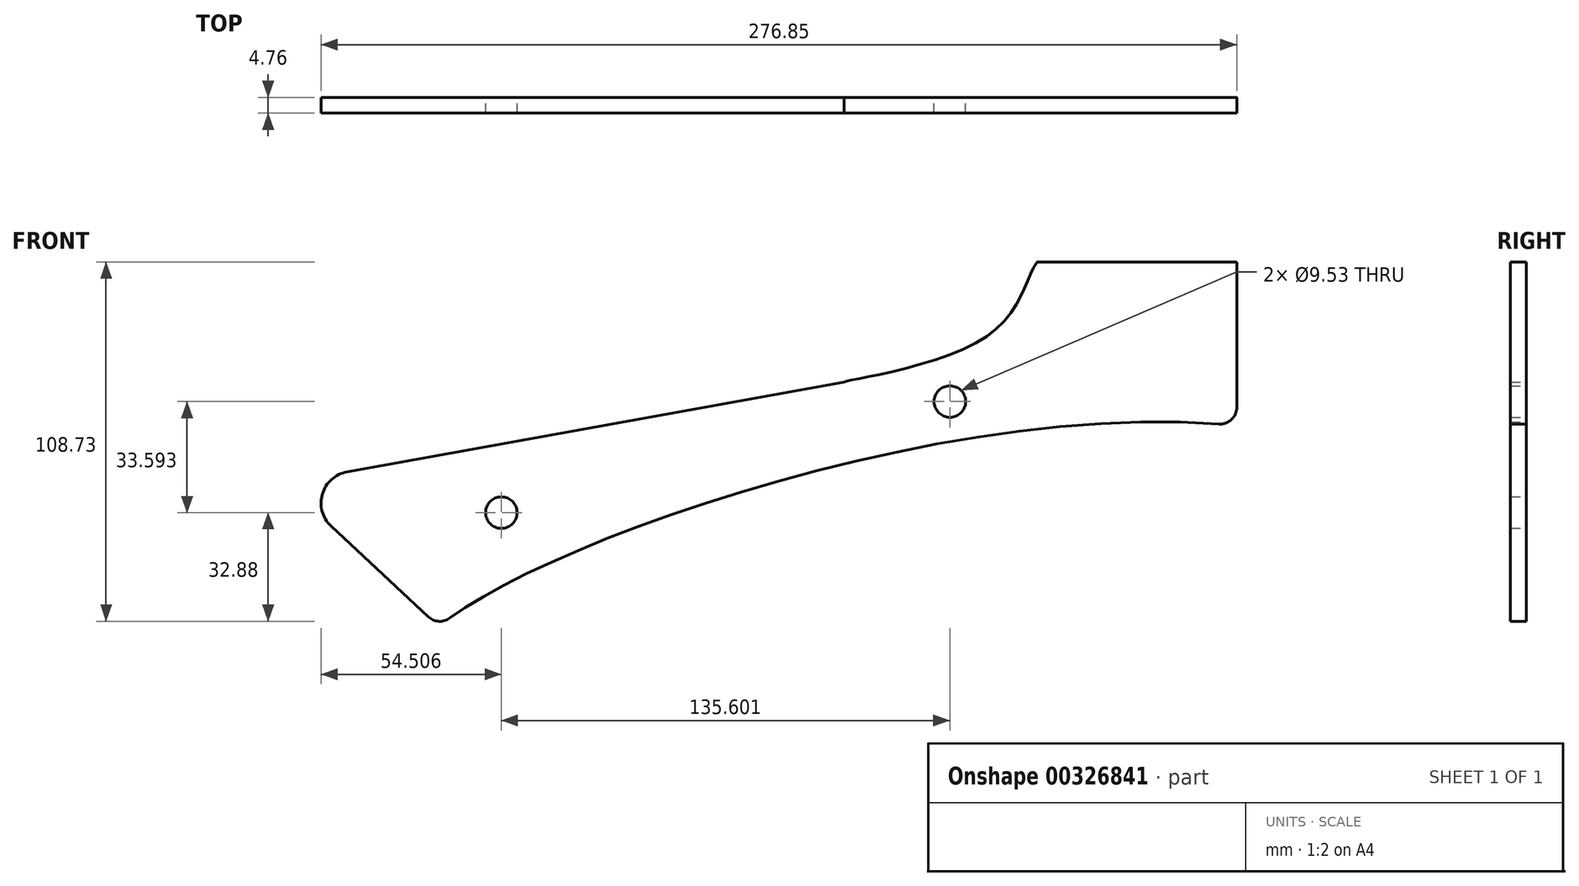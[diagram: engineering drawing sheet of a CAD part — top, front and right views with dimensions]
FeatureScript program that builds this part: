
annotation { "Feature Type Name" : "Feature", "Feature Type Description" : "" }
export const myFeature = defineFeature(function(context is Context, id is Id, definition is map)
    precondition{}
    {
        {
            var Q0;
            Q0=qCreatedBy(makeId("Front.planeOp"),FACE);
            var sketch = newSketch(context, id + "F0", { "sketchPlane" : qUnion([Q0])});
            skLineSegment(sketch, "E0", {"start": v(-108.84, -14.05) * mm, "end": v(-62.45, -57.41) * mm});
            skFitSpline(sketch, "E1", {"points": [v(-62.45, -57.41) * mm, v(6.41, -24.14) * mm, v(178.85, 3.34) * mm], "startDerivative": vector(92.55, 74.48) * mm, "endDerivative": vector(274.58, -28.19) * mm});
            skLineSegment(sketch, "E2", {"start": v(178.85, 3.34) * mm, "end": v(178.85, 52.87) * mm});
            skLineSegment(sketch, "E3", {"start": v(178.85, 52.87) * mm, "end": v(118.52, 52.87) * mm});
            skCircle(sketch, "E4", {"center": v(-43.5, -22.98) * mm, "radius": 4.76 * mm});
            skCircle(sketch, "E5", {"center": v(92.1, 10.61) * mm, "radius": 4.76 * mm});
            skPoint(sketch, "E6.1.internal.orphan", {"position": v(26.94, 0) * mm});
            skFitSpline(sketch, "E7", {"points": [v(118.52, 52.87) * mm, v(103.5, 30.5) * mm, v(60.14, 16.53) * mm], "startDerivative": vector(-23.35, -31.87) * mm, "endDerivative": vector(-4.02, -3.66) * mm});
            skLineSegment(sketch, "E8", {"start": v(-43.5, -22.98) * mm, "end": v(92.1, 10.61) * mm, "construction": true});
            skLineSegment(sketch, "E9", {"start": v(60.14, 16.53) * mm, "end": v(-108.84, -14.05) * mm});
            skSolve(sketch);
        }
        {
            var Q0;
            Q0=qSketchRegion(id+"F0",true);
            extrude(context, id + "F1", {"entities" : qUnion([Q0]), "depth" : 4.76 * mm});
        }
        {
            var Q0;
            Q0=makeQuery(id+"F1.opExtrude","SWEPT_EDGE",EDGE,{"disambiguationData":[OSD([sQuery(id+"F0.wireOp",EDGE,"E0"),sQuery(id+"F0.wireOp",EDGE,"E1")])]});
            var Q1;
            Q1=makeQuery(id+"F1.opExtrude","SWEPT_EDGE",EDGE,{"disambiguationData":[OSD([sQuery(id+"F0.wireOp",EDGE,"E1"),sQuery(id+"F0.wireOp",EDGE,"E2")])]});
            fillet(context, id + "F2", {"entities" : qUnion([Q0, Q1]), "radius" : 5.08 * mm, "tangentPropagation" : true, "allowEdgeOverflow" : false});
        }
        {
            var Q0;
            Q0=makeQuery(id+"F1.opExtrude","SWEPT_EDGE",EDGE,{"disambiguationData":[OSD([sQuery(id+"F0.wireOp",EDGE,"E0"),sQuery(id+"F0.wireOp",EDGE,"E9")])]});
            fillet(context, id + "F3", {"entities" : qUnion([Q0]), "radius" : 9.52 * mm, "tangentPropagation" : true, "allowEdgeOverflow" : false});
        }
        {
            var Q0;
            Q0=makeQuery(id+"F1.opExtrude","SWEPT_EDGE",EDGE,{"disambiguationData":[OSD([sQuery(id+"F0.wireOp",EDGE,"E2"),sQuery(id+"F0.wireOp",EDGE,"E3")])]});
            var Q1;
            Q1=makeQuery(id+"F1.opExtrude","SWEPT_EDGE",EDGE,{"disambiguationData":[OSD([sQuery(id+"F0.wireOp",EDGE,"E3"),sQuery(id+"F0.wireOp",EDGE,"E7")])]});
            fillet(context, id + "F4", {"entities" : qUnion([Q0, Q1]), "radius" : 0.38 * mm, "tangentPropagation" : true, "allowEdgeOverflow" : false});
        }
    });
